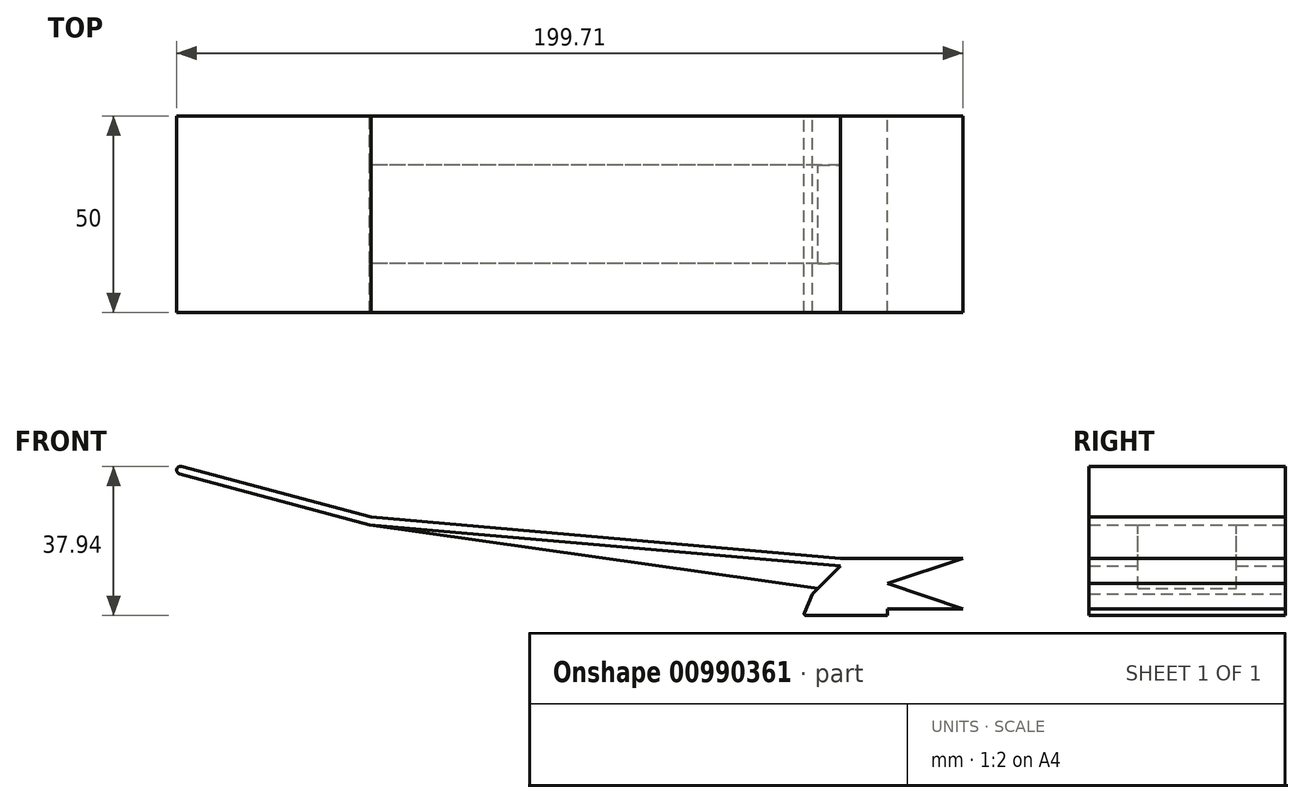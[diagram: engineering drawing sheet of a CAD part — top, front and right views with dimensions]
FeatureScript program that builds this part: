
annotation { "Feature Type Name" : "Feature", "Feature Type Description" : "" }
export const myFeature = defineFeature(function(context is Context, id is Id, definition is map)
    precondition{}
    {
        {
            var Q0;
            Q0=qCreatedBy(makeId("Front.planeOp"),FACE);
            var sketch = newSketch(context, id + "F0", { "sketchPlane" : qUnion([Q0])});
            skLineSegment(sketch, "E0", {"start": v(26.32, -11.58) * mm, "end": v(28.37, -6.78) * mm});
            skPoint(sketch, "E1.visualSharp", {"position": v(26.02, -12.28) * mm});
            skArc(sketch, "E1.filletArc", {"start": v(26.32, -11.58) * mm, "mid": v(26.36, -12.05) * mm, "end": v(26.78, -12.28) * mm});
            skLineSegment(sketch, "E2", {"start": v(26.78, -12.28) * mm, "end": v(47.48, -12.28) * mm});
            skLineSegment(sketch, "E3", {"start": v(47.48, -12.28) * mm, "end": v(47.48, -10.58) * mm});
            skLineSegment(sketch, "E4", {"start": v(47.48, -10.58) * mm, "end": v(66.57, -10.58) * mm});
            skLineSegment(sketch, "E5", {"start": v(28.37, -6.78) * mm, "end": v(35.44, 0.3) * mm});
            skLineSegment(sketch, "E6", {"start": v(35.44, 0.3) * mm, "end": v(-84.1, 10.75) * mm});
            skLineSegment(sketch, "E7", {"start": v(-84.1, 10.75) * mm, "end": v(-132.4, 23.7) * mm});
            skLineSegment(sketch, "E8.0", {"start": v(-83.75, 12.73) * mm, "end": v(-131.88, 25.63) * mm});
            skLineSegment(sketch, "E8.3", {"start": v(35.53, 2.3) * mm, "end": v(66.57, 2.3) * mm});
            skLineSegment(sketch, "E8.4", {"start": v(35.53, 2.3) * mm, "end": v(-83.75, 12.73) * mm});
            skArc(sketch, "E9", {"start": v(-131.88, 25.63) * mm, "mid": v(-133.1, 24.92) * mm, "end": v(-132.4, 23.7) * mm});
            skLineSegment(sketch, "E10", {"start": v(29.79, -5.36) * mm, "end": v(-84.1, 10.75) * mm});
            skLineSegment(sketch, "E11", {"start": v(66.57, 2.3) * mm, "end": v(47.48, -4.14) * mm});
            skLineSegment(sketch, "E12", {"start": v(47.48, -4.14) * mm, "end": v(66.57, -10.58) * mm});
            skSolve(sketch);
        }
        {
            var Q0;
            {var subQ3=sQuery(id+"F0.wireOp",EDGE,"E0");Q0=makeQuery(id+"F0.imprint","IMPRINT",FACE,{"disambiguationData":[TD([[makeQuery(id+"F0.imprint","IMPRINT",EDGE,{"derivedFrom":subQ3}),-1.0]])]});}
            extrude(context, id + "F1", {"entities" : qUnion([Q0]), "endBound" : BoundingType.SYMMETRIC, "depth" : 50 * mm, "offsetDistance" : 25 * mm});
        }
        {
            var Q0;
            {var subQ0=sQuery(id+"F0.wireOp",EDGE,"E6");Q0=makeQuery(id+"F0.imprint","IMPRINT",FACE,{"disambiguationData":[TD([[makeQuery(id+"F0.imprint","IMPRINT",EDGE,{"derivedFrom":subQ0}),1.0]])]});}
            extrude(context, id + "F2", {"entities" : qUnion([Q0]), "operationType" : NewBodyOperationType.ADD, "endBound" : BoundingType.SYMMETRIC, "depth" : 25 * mm, "offsetDistance" : 25 * mm});
        }
        {
            var Q0;
            Q0=makeQuery(id+"F1.opExtrude","SWEPT_FACE",FACE,{"disambiguationData":[OSD([sQuery(id+"F0.wireOp",EDGE,"E8.4")])]});
            cPlane(context, id + "F3", {"entities" : qUnion([Q0]), "cplaneType" : CPlaneType.OFFSET, "offset" : 0 * mm, "width" : 150 * mm, "height" : 150 * mm});
        }
    });
